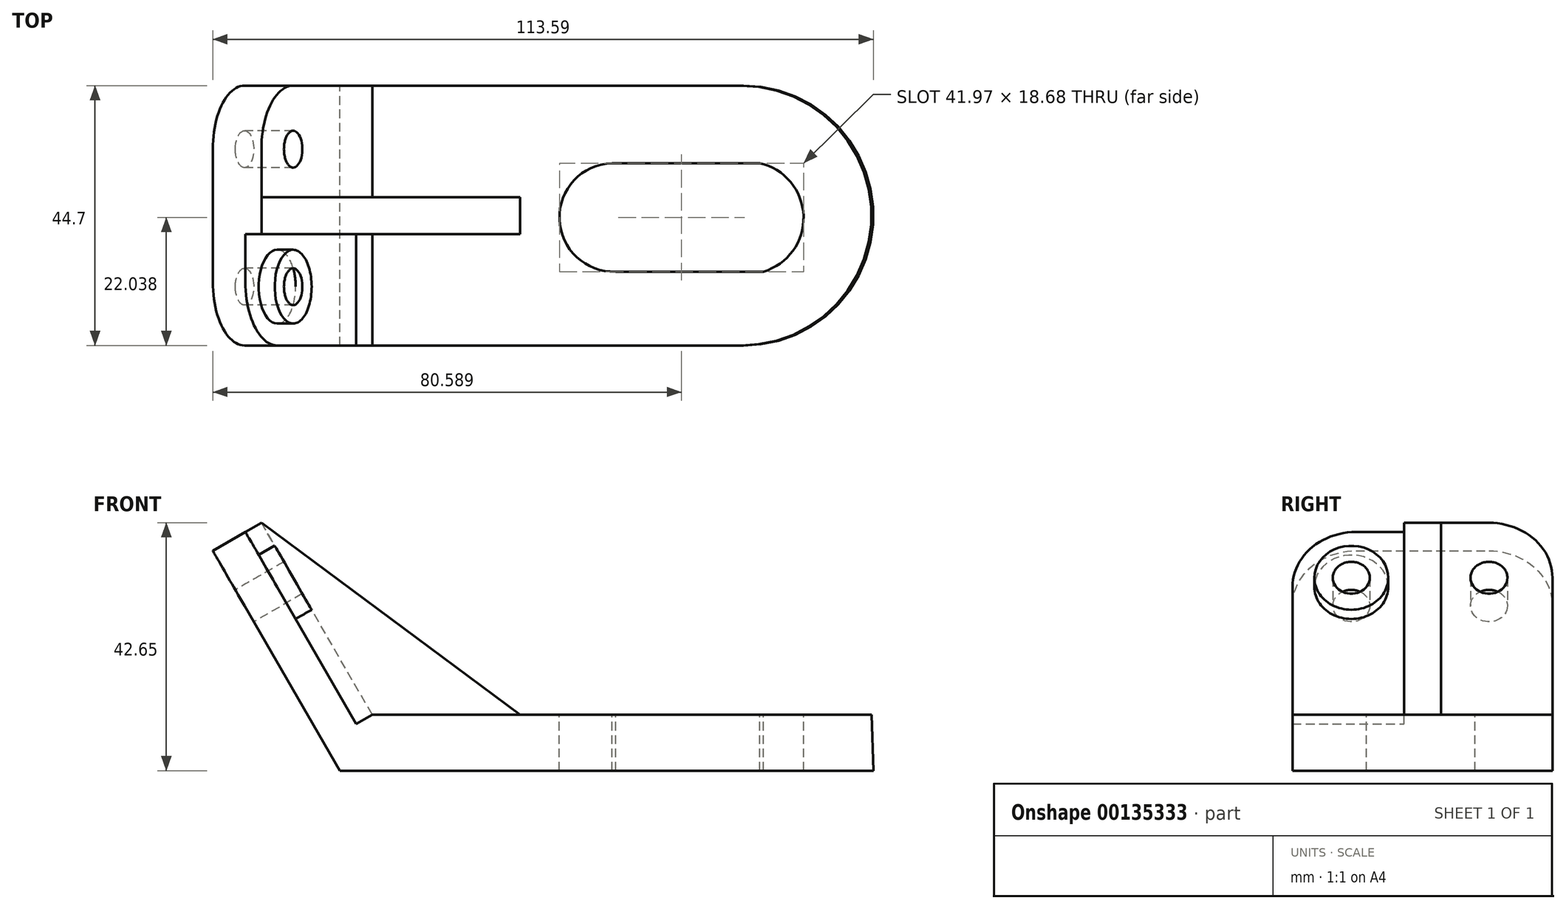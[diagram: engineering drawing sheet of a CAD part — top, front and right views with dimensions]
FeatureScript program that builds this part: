
annotation { "Feature Type Name" : "Feature", "Feature Type Description" : "" }
export const myFeature = defineFeature(function(context is Context, id is Id, definition is map)
    precondition{}
    {
        {
            var Q0;
            Q0=qCreatedBy(makeId("Front.planeOp"),FACE);
            var sketch = newSketch(context, id + "F0", { "sketchPlane" : qUnion([Q0])});
            skLineSegment(sketch, "E0", {"start": v(-29.34, 0) * mm, "end": v(-48.4, 33) * mm});
            skLineSegment(sketch, "E1", {"start": v(-34.92, -9.65) * mm, "end": v(-56.75, 28.17) * mm});
            skLineSegment(sketch, "E2", {"start": v(-48.4, 33) * mm, "end": v(-56.75, 28.17) * mm});
            skLineSegment(sketch, "E3", {"start": v(-48.4, 33) * mm, "end": v(-3.94, 0) * mm});
            skLineSegment(sketch, "E4", {"start": v(-29.34, 0) * mm, "end": v(56.5, 0) * mm});
            skLineSegment(sketch, "E5", {"start": v(-34.92, -9.65) * mm, "end": v(56.84, -9.65) * mm});
            skLineSegment(sketch, "E6", {"start": v(56.5, 0) * mm, "end": v(56.84, -9.65) * mm});
            skSolve(sketch);
        }
        {
            var Q0;
            {var subQ1=sQuery(id+"F0.wireOp",EDGE,"E0");Q0=makeQuery(id+"F0.imprint","IMPRINT",FACE,{"disambiguationData":[TD([[makeQuery(id+"F0.imprint","IMPRINT",EDGE,{"derivedFrom":subQ1}),1.0]])]});}
            extrude(context, id + "F1", {"entities" : qUnion([Q0]), "endBound" : BoundingType.SYMMETRIC, "depth" : 44.7 * mm});
        }
        {
            var Q0;
            {var subQ0=sQuery(id+"F0.wireOp",EDGE,"E0");Q0=makeQuery(id+"F0.imprint","IMPRINT",FACE,{"disambiguationData":[TD([[makeQuery(id+"F0.imprint","IMPRINT",EDGE,{"derivedFrom":subQ0}),-1.0]])]});}
            extrude(context, id + "F2", {"entities" : qUnion([Q0]), "operationType" : NewBodyOperationType.ADD, "endBound" : BoundingType.SYMMETRIC, "depth" : 6.35 * mm});
        }
        {
            var Q0;
            Q0=makeQuery(id+"F1.opExtrude","SWEPT_FACE",FACE,{"disambiguationData":[OSD([sQuery(id+"F0.wireOp",EDGE,"E4")])]});
            var sketch = newSketch(context, id + "F3", { "sketchPlane" : qUnion([Q0])});
            skLineSegment(sketch, "E7", {"start": v(11.87, 9.03) * mm, "end": v(37.27, 9.03) * mm});
            skLineSegment(sketch, "E8", {"start": v(37.91, -9.65) * mm, "end": v(12.51, -9.65) * mm});
            skArc(sketch, "E9", {"start": v(11.87, 9.03) * mm, "mid": v(2.85, -0.63) * mm, "end": v(12.51, -9.65) * mm});
            skArc(sketch, "E10", {"start": v(37.91, -9.65) * mm, "mid": v(44.83, -0.06) * mm, "end": v(37.27, 9.03) * mm});
            skSolve(sketch);
        }
        {
            var Q0;
            Q0=makeQuery(id+"F1.opExtrude","CAP_EDGE",EDGE,{"disambiguationData":[OSD([sQuery(id+"F0.wireOp",EDGE,"E6")])],"isStart":false});
            var Q1;
            Q1=makeQuery(id+"F1.opExtrude","CAP_EDGE",EDGE,{"disambiguationData":[OSD([sQuery(id+"F0.wireOp",EDGE,"E6")])],"isStart":true});
            fillet(context, id + "F4", {"entities" : qUnion([Q0, Q1]), "radius" : 22.35 * mm, "tangentPropagation" : true, "allowEdgeOverflow" : false});
        }
        {
            var Q0;
            Q0=makeQuery(id+"F1.opExtrude","SWEPT_FACE",FACE,{"disambiguationData":[OSD([sQuery(id+"F0.wireOp",EDGE,"E1")])]});
            var sketch = newSketch(context, id + "F5", { "sketchPlane" : qUnion([Q0])});
            skCircle(sketch, "E11", {"center": v(-11.43, 41.85) * mm, "radius": 6.35 * mm});
            skCircle(sketch, "E12", {"center": v(12.24, 41.85) * mm, "radius": 6.35 * mm});
            skCircle(sketch, "E13", {"center": v(12.24, 41.85) * mm, "radius": 3.18 * mm});
            skCircle(sketch, "E14", {"center": v(-11.43, 41.85) * mm, "radius": 3.18 * mm});
            skSolve(sketch);
        }
        {
            var Q0;
            Q0=makeQuery(id+"F5.imprint","IMPRINT",FACE,{"disambiguationData":[TD([[makeQuery(id+"F5.imprint","IMPRINT",EDGE,{"derivedFrom":sQuery(id+"F5.wireOp",EDGE,"E14")}),1.0]])]});
            var Q1;
            Q1=makeQuery(id+"F5.imprint","IMPRINT",FACE,{"disambiguationData":[TD([[makeQuery(id+"F5.imprint","IMPRINT",EDGE,{"derivedFrom":sQuery(id+"F5.wireOp",EDGE,"E13")}),1.0]])]});
            extrude(context, id + "F6", {"entities" : qUnion([Q0, Q1]), "operationType" : NewBodyOperationType.REMOVE, "oppositeDirection" : true, "depth" : 25.4 * mm});
        }
        {
            var Q0;
            {var subQ0=sQuery(id+"F0.wireOp",EDGE,"E4");var subQ1=sQuery(id+"F0.wireOp",EDGE,"E3");var subQ2=sQuery(id+"F0.wireOp",EDGE,"E0");Q0=makeQuery(id+"F2.boolean.opBoolean","SPLIT",FACE,{"disambiguationData":[TD([makeQuery(id+"F2.opExtrude","CAP_FACE",FACE,{"disambiguationData":[OSD([subQ2,subQ1,subQ0])],"isStart":false})])],"derivedFrom":makeQuery(id+"F1.opExtrude","SWEPT_FACE",FACE,{"disambiguationData":[OSD([subQ2])]})});}
            var sketch = newSketch(context, id + "F7", { "sketchPlane" : qUnion([Q0])});
            skCircle(sketch, "E15.0", {"center": v(-12.24, 41.85) * mm, "radius": 6.35 * mm});
            skCircle(sketch, "E16.0", {"center": v(11.43, 41.85) * mm, "radius": 6.35 * mm});
            skSolve(sketch);
        }
        {
            var Q0;
            Q0=makeQuery(id+"F7.imprint","IMPRINT",FACE,{"disambiguationData":[TD([[makeQuery(id+"F7.imprint","IMPRINT",EDGE,{"derivedFrom":sQuery(id+"F7.wireOp",EDGE,"E15.0")}),-1.0]])]});
            var Q1;
            Q1=makeQuery(id+"F7.imprint","IMPRINT",FACE,{"disambiguationData":[TD([[makeQuery(id+"F7.imprint","IMPRINT",EDGE,{"derivedFrom":sQuery(id+"F7.wireOp",EDGE,"E16.0")}),-1.0]])]});
            extrude(context, id + "F8", {"entities" : qUnion([Q0, Q1]), "operationType" : NewBodyOperationType.REMOVE, "oppositeDirection" : true, "depth" : 3.17 * mm});
        }
        {
            var Q0;
            Q0=makeQuery(id+"F1.opExtrude","CAP_EDGE",EDGE,{"disambiguationData":[OSD([sQuery(id+"F0.wireOp",EDGE,"E2")])],"isStart":true});
            var Q1;
            Q1=makeQuery(id+"F1.opExtrude","CAP_EDGE",EDGE,{"disambiguationData":[OSD([sQuery(id+"F0.wireOp",EDGE,"E2")])],"isStart":false});
            fillet(context, id + "F9", {"entities" : qUnion([Q0, Q1]), "radius" : 10.92 * mm, "tangentPropagation" : true, "allowEdgeOverflow" : false});
        }
        {
            var Q0;
            Q0=makeQuery(id+"F3.imprint","IMPRINT",FACE,{"disambiguationData":[TD([[makeQuery(id+"F3.imprint","IMPRINT",EDGE,{"derivedFrom":sQuery(id+"F3.wireOp",EDGE,"E7")}),-1.0]])]});
            extrude(context, id + "F10", {"entities" : qUnion([Q0]), "operationType" : NewBodyOperationType.REMOVE, "oppositeDirection" : true, "depth" : 25.4 * mm});
        }
    });
